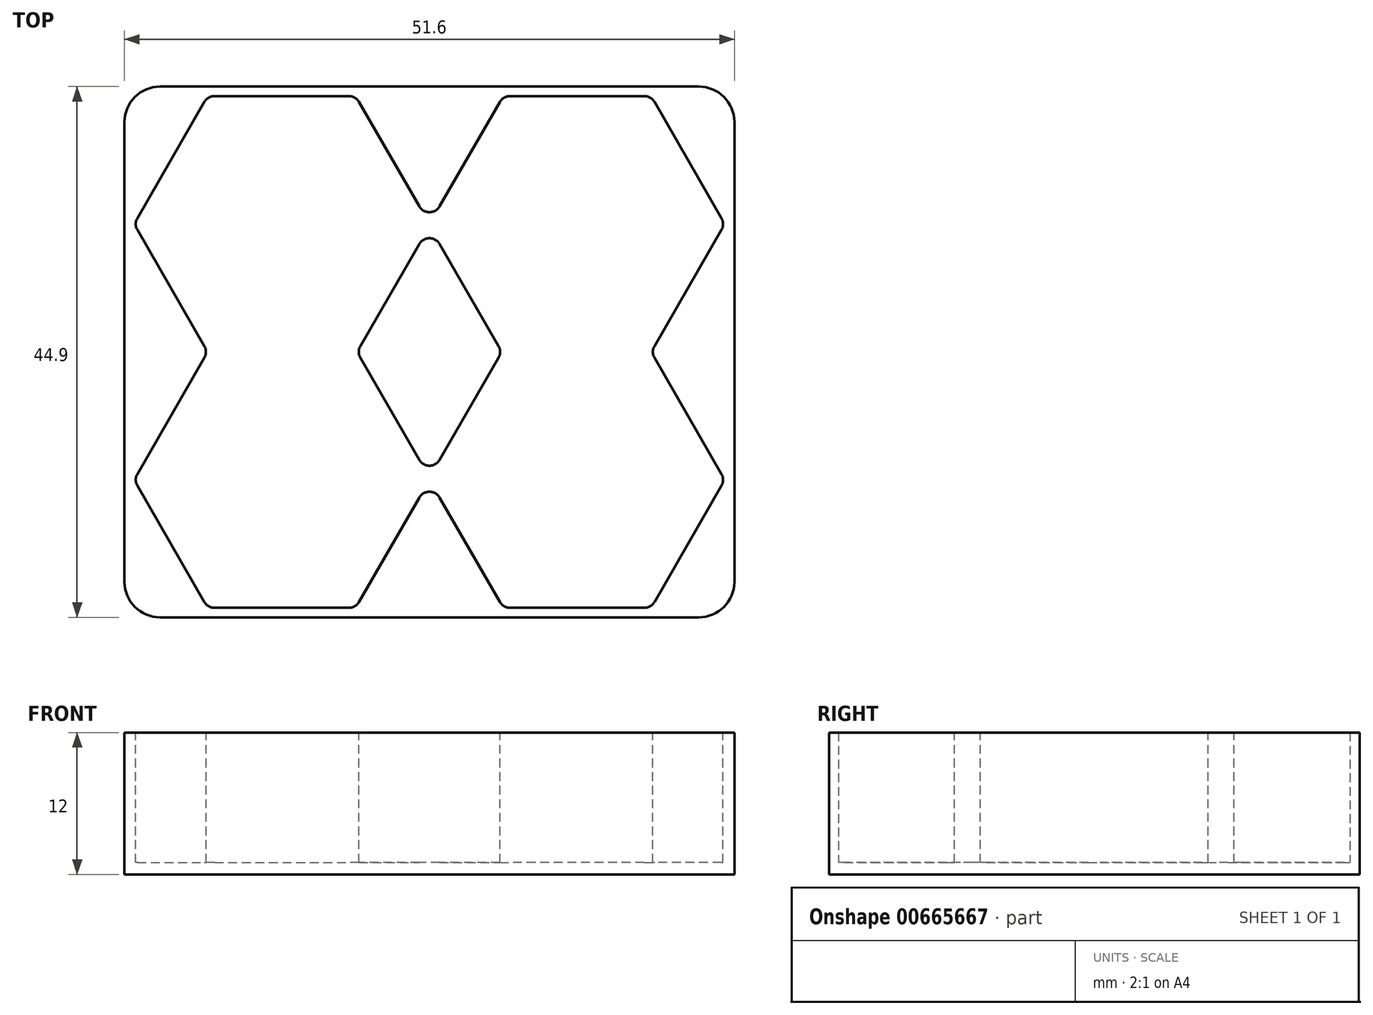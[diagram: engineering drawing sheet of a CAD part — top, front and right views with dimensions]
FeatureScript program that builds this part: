
annotation { "Feature Type Name" : "Feature", "Feature Type Description" : "" }
export const myFeature = defineFeature(function(context is Context, id is Id, definition is map)
    precondition{}
    {
        {
            var Q0;
            Q0=qCreatedBy(makeId("Top.planeOp"),FACE);
            var sketch = newSketch(context, id + "F0", { "sketchPlane" : qUnion([Q0])});
            skLineSegment(sketch, "E0.bottom", {"start": v(25, -21.65) * mm, "end": v(-25, -21.65) * mm, "construction": true});
            skLineSegment(sketch, "E0.top", {"start": v(25, 21.65) * mm, "end": v(-25, 21.65) * mm, "construction": true});
            skLineSegment(sketch, "E0.left", {"start": v(25, -21.65) * mm, "end": v(25, 21.65) * mm, "construction": true});
            skLineSegment(sketch, "E0.right", {"start": v(-25, -21.65) * mm, "end": v(-25, 21.65) * mm, "construction": true});
            skPoint(sketch, "E0.middle", {"position": v(0, 0) * mm});
            skLineSegment(sketch, "E1", {"start": v(25, 10.83) * mm, "end": v(18.75, 21.65) * mm});
            skLineSegment(sketch, "E2", {"start": v(18.75, 21.65) * mm, "end": v(6.25, 21.65) * mm});
            skLineSegment(sketch, "E3", {"start": v(6.25, 21.65) * mm, "end": v(0, 10.83) * mm});
            skLineSegment(sketch, "E4", {"start": v(0, 10.83) * mm, "end": v(6.25, 0) * mm, "construction": true});
            skLineSegment(sketch, "E5", {"start": v(18.75, 0) * mm, "end": v(25, 10.83) * mm});
            skLineSegment(sketch, "E6.MirrorCS", {"start": v(0, 10.83) * mm, "end": v(-6.25, 0) * mm, "construction": true});
            skLineSegment(sketch, "E7.MirrorCS", {"start": v(-6.25, 21.65) * mm, "end": v(0, 10.83) * mm});
            skLineSegment(sketch, "E8.MirrorCS", {"start": v(-25, 10.83) * mm, "end": v(-18.75, 21.65) * mm});
            skLineSegment(sketch, "E9.MirrorCS", {"start": v(-18.75, 0) * mm, "end": v(-25, 10.83) * mm});
            skLineSegment(sketch, "E10.MirrorCS", {"start": v(0, -10.83) * mm, "end": v(6.25, 0) * mm, "construction": true});
            skLineSegment(sketch, "E11.MirrorCS", {"start": v(6.25, -21.65) * mm, "end": v(0, -10.83) * mm});
            skLineSegment(sketch, "E12.MirrorCS", {"start": v(-6.25, -21.65) * mm, "end": v(0, -10.83) * mm});
            skLineSegment(sketch, "E13.MirrorCS", {"start": v(0, -10.83) * mm, "end": v(-6.25, 0) * mm, "construction": true});
            skLineSegment(sketch, "E14.MirrorCS", {"start": v(-18.75, 0) * mm, "end": v(-25, -10.83) * mm});
            skLineSegment(sketch, "E15.MirrorCS", {"start": v(-25, -10.83) * mm, "end": v(-18.75, -21.65) * mm});
            skLineSegment(sketch, "E16.MirrorCS", {"start": v(25, -10.83) * mm, "end": v(18.75, -21.65) * mm});
            skLineSegment(sketch, "E17.MirrorCS", {"start": v(18.75, 0) * mm, "end": v(25, -10.83) * mm});
            skLineSegment(sketch, "E18.0", {"start": v(25.8, 22.45) * mm, "end": v(-25.8, 22.45) * mm});
            skLineSegment(sketch, "E18.1", {"start": v(25.8, -22.45) * mm, "end": v(25.8, 22.45) * mm});
            skLineSegment(sketch, "E18.2", {"start": v(25.8, -22.45) * mm, "end": v(-25.8, -22.45) * mm});
            skLineSegment(sketch, "E18.3", {"start": v(-25.8, -22.45) * mm, "end": v(-25.8, 22.45) * mm});
            skLineSegment(sketch, "E19.0", {"start": v(0, 10.63) * mm, "end": v(-6.13, 0) * mm});
            skLineSegment(sketch, "E19.1", {"start": v(0, 10.63) * mm, "end": v(6.13, 0) * mm});
            skLineSegment(sketch, "E19.2", {"start": v(0, -10.63) * mm, "end": v(6.13, 0) * mm});
            skLineSegment(sketch, "E19.3", {"start": v(0, -10.63) * mm, "end": v(-6.13, 0) * mm});
            skLineSegment(sketch, "E20.MirrorCS", {"start": v(-18.75, 21.65) * mm, "end": v(-6.25, 21.65) * mm});
            skLineSegment(sketch, "E21.MirrorCS", {"start": v(-18.75, -21.65) * mm, "end": v(-6.25, -21.65) * mm});
            skLineSegment(sketch, "E22.MirrorCS", {"start": v(18.75, -21.65) * mm, "end": v(6.25, -21.65) * mm});
            skSolve(sketch);
        }
        {
            var Q0;
            Q0=makeQuery(id+"F0.imprint","IMPRINT",FACE,{"disambiguationData":[TD([[makeQuery(id+"F0.imprint","IMPRINT",EDGE,{"derivedFrom":sQuery(id+"F0.wireOp",EDGE,"E1")}),1.0]])]});
            extrude(context, id + "F1", {"entities" : qUnion([Q0]), "depth" : 1 * mm, "offsetDistance" : 25 * mm});
        }
        {
            var Q0;
            Q0=makeQuery(id+"F0.imprint","IMPRINT",FACE,{"disambiguationData":[TD([[makeQuery(id+"F0.imprint","IMPRINT",EDGE,{"derivedFrom":sQuery(id+"F0.wireOp",EDGE,"E1")}),-1.0]])]});
            var Q1;
            Q1=makeQuery(id+"F0.imprint","IMPRINT",FACE,{"disambiguationData":[TD([[makeQuery(id+"F0.imprint","IMPRINT",EDGE,{"derivedFrom":sQuery(id+"F0.wireOp",EDGE,"E19.0")}),1.0]])]});
            extrude(context, id + "F2", {"entities" : qUnion([Q0, Q1]), "operationType" : NewBodyOperationType.ADD, "depth" : 12 * mm, "offsetDistance" : 25 * mm});
        }
        {
            var Q0;
            Q0=makeQuery(id+"F2.opExtrude","SWEPT_EDGE",EDGE,{"disambiguationData":[OSD([sQuery(id+"F0.wireOp",EDGE,"E18.1"),sQuery(id+"F0.wireOp",EDGE,"E18.2")])]});
            var Q1;
            Q1=makeQuery(id+"F2.opExtrude","SWEPT_EDGE",EDGE,{"disambiguationData":[OSD([sQuery(id+"F0.wireOp",EDGE,"E18.0"),sQuery(id+"F0.wireOp",EDGE,"E18.1")])]});
            var Q2;
            Q2=makeQuery(id+"F2.opExtrude","SWEPT_EDGE",EDGE,{"disambiguationData":[OSD([sQuery(id+"F0.wireOp",EDGE,"E18.2"),sQuery(id+"F0.wireOp",EDGE,"E18.3")])]});
            var Q3;
            Q3=makeQuery(id+"F2.opExtrude","SWEPT_EDGE",EDGE,{"disambiguationData":[OSD([sQuery(id+"F0.wireOp",EDGE,"E18.0"),sQuery(id+"F0.wireOp",EDGE,"E18.3")])]});
            fillet(context, id + "F3", {"entities" : qUnion([Q0, Q1, Q2, Q3]), "radius" : 3 * mm, "tangentPropagation" : true, "allowEdgeOverflow" : false});
        }
        {
            var Q0;
            Q0=makeQuery(id+"F2.opExtrude","SWEPT_EDGE",EDGE,{"disambiguationData":[OSD([sQuery(id+"F0.wireOp",EDGE,"E11.MirrorCS"),sQuery(id+"F0.wireOp",EDGE,"E12.MirrorCS")])]});
            var Q1;
            Q1=makeQuery(id+"F2.opExtrude","SWEPT_EDGE",EDGE,{"disambiguationData":[OSD([sQuery(id+"F0.wireOp",EDGE,"E19.2"),sQuery(id+"F0.wireOp",EDGE,"E19.3")])]});
            var Q2;
            Q2=makeQuery(id+"F2.opExtrude","SWEPT_EDGE",EDGE,{"disambiguationData":[OSD([sQuery(id+"F0.wireOp",EDGE,"E19.1"),sQuery(id+"F0.wireOp",EDGE,"E19.2")])]});
            var Q3;
            Q3=makeQuery(id+"F2.opExtrude","SWEPT_EDGE",EDGE,{"disambiguationData":[OSD([sQuery(id+"F0.wireOp",EDGE,"E3"),sQuery(id+"F0.wireOp",EDGE,"E7.MirrorCS")])]});
            var Q4;
            Q4=makeQuery(id+"F2.opExtrude","SWEPT_EDGE",EDGE,{"disambiguationData":[OSD([sQuery(id+"F0.wireOp",EDGE,"E19.0"),sQuery(id+"F0.wireOp",EDGE,"E19.1")])]});
            var Q5;
            Q5=makeQuery(id+"F2.opExtrude","SWEPT_EDGE",EDGE,{"disambiguationData":[OSD([sQuery(id+"F0.wireOp",EDGE,"E8.MirrorCS"),sQuery(id+"F0.wireOp",EDGE,"E9.MirrorCS")])]});
            var Q6;
            Q6=makeQuery(id+"F2.opExtrude","SWEPT_EDGE",EDGE,{"disambiguationData":[OSD([sQuery(id+"F0.wireOp",EDGE,"E9.MirrorCS"),sQuery(id+"F0.wireOp",EDGE,"E14.MirrorCS")])]});
            var Q7;
            Q7=makeQuery(id+"F2.opExtrude","SWEPT_EDGE",EDGE,{"disambiguationData":[OSD([sQuery(id+"F0.wireOp",EDGE,"E14.MirrorCS"),sQuery(id+"F0.wireOp",EDGE,"E15.MirrorCS")])]});
            var Q8;
            Q8=makeQuery(id+"F2.opExtrude","SWEPT_EDGE",EDGE,{"disambiguationData":[OSD([sQuery(id+"F0.wireOp",EDGE,"E19.0"),sQuery(id+"F0.wireOp",EDGE,"E19.3")])]});
            var Q9;
            Q9=makeQuery(id+"F2.opExtrude","SWEPT_EDGE",EDGE,{"disambiguationData":[OSD([sQuery(id+"F0.wireOp",EDGE,"E15.MirrorCS"),sQuery(id+"F0.wireOp",EDGE,"E21.MirrorCS")])]});
            var Q10;
            Q10=makeQuery(id+"F2.opExtrude","SWEPT_EDGE",EDGE,{"disambiguationData":[OSD([sQuery(id+"F0.wireOp",EDGE,"E12.MirrorCS"),sQuery(id+"F0.wireOp",EDGE,"E21.MirrorCS")])]});
            var Q11;
            Q11=makeQuery(id+"F2.opExtrude","SWEPT_EDGE",EDGE,{"disambiguationData":[OSD([sQuery(id+"F0.wireOp",EDGE,"E7.MirrorCS"),sQuery(id+"F0.wireOp",EDGE,"E20.MirrorCS")])]});
            var Q12;
            Q12=makeQuery(id+"F2.opExtrude","SWEPT_EDGE",EDGE,{"disambiguationData":[OSD([sQuery(id+"F0.wireOp",EDGE,"E8.MirrorCS"),sQuery(id+"F0.wireOp",EDGE,"E20.MirrorCS")])]});
            var Q13;
            Q13=makeQuery(id+"F2.opExtrude","SWEPT_EDGE",EDGE,{"disambiguationData":[OSD([sQuery(id+"F0.wireOp",EDGE,"E11.MirrorCS"),sQuery(id+"F0.wireOp",EDGE,"E22.MirrorCS")])]});
            var Q14;
            Q14=makeQuery(id+"F2.opExtrude","SWEPT_EDGE",EDGE,{"disambiguationData":[OSD([sQuery(id+"F0.wireOp",EDGE,"E16.MirrorCS"),sQuery(id+"F0.wireOp",EDGE,"E22.MirrorCS")])]});
            var Q15;
            Q15=makeQuery(id+"F2.opExtrude","SWEPT_EDGE",EDGE,{"disambiguationData":[OSD([sQuery(id+"F0.wireOp",EDGE,"E5"),sQuery(id+"F0.wireOp",EDGE,"E17.MirrorCS")])]});
            var Q16;
            Q16=makeQuery(id+"F2.opExtrude","SWEPT_EDGE",EDGE,{"disambiguationData":[OSD([sQuery(id+"F0.wireOp",EDGE,"E2"),sQuery(id+"F0.wireOp",EDGE,"E3")])]});
            var Q17;
            Q17=makeQuery(id+"F2.opExtrude","SWEPT_EDGE",EDGE,{"disambiguationData":[OSD([sQuery(id+"F0.wireOp",EDGE,"E1"),sQuery(id+"F0.wireOp",EDGE,"E2")])]});
            var Q18;
            Q18=makeQuery(id+"F2.opExtrude","SWEPT_EDGE",EDGE,{"disambiguationData":[OSD([sQuery(id+"F0.wireOp",EDGE,"E1"),sQuery(id+"F0.wireOp",EDGE,"E5")])]});
            var Q19;
            Q19=makeQuery(id+"F2.opExtrude","SWEPT_EDGE",EDGE,{"disambiguationData":[OSD([sQuery(id+"F0.wireOp",EDGE,"E16.MirrorCS"),sQuery(id+"F0.wireOp",EDGE,"E17.MirrorCS")])]});
            fillet(context, id + "F4", {"entities" : qUnion([Q0, Q1, Q2, Q3, Q4, Q5, Q6, Q7, Q8, Q9, Q10, Q11, Q12, Q13, Q14, Q15, Q16, Q17, Q18, Q19]), "radius" : 1 * mm, "tangentPropagation" : true, "allowEdgeOverflow" : false});
        }
    });
